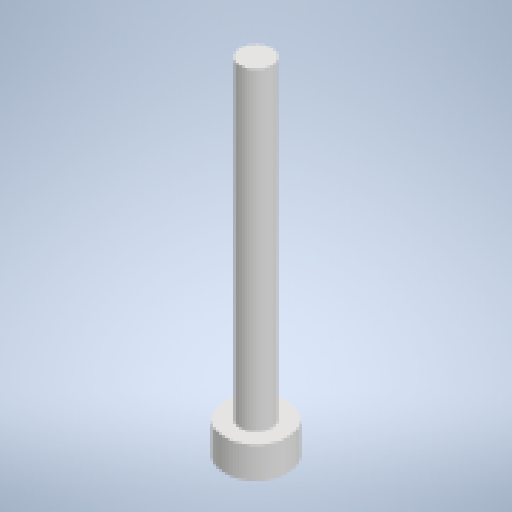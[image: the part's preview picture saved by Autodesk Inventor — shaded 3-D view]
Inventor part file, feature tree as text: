
AUTODESK INVENTOR PART (.ipt)
format: ipt  version: 2024.2 (Build 282272000, 272)  size: 121,856 bytes
history: native  units: mm
features: extrude x2, other x1, sketch x1
ambient origin geometry x8: Origin, YZ Plane, XZ Plane, XY Plane, X Axis, Y Axis, Z Axis, Center Point
bodies: Body1 (feature_tree)
feature tree (4):
  other  "Твердое тело1"
  sketch  "Эскиз1"
  extrude  "Выдавливание1"  Depth=10.0mm
  extrude  "Выдавливание2"  Depth=5.0mm
